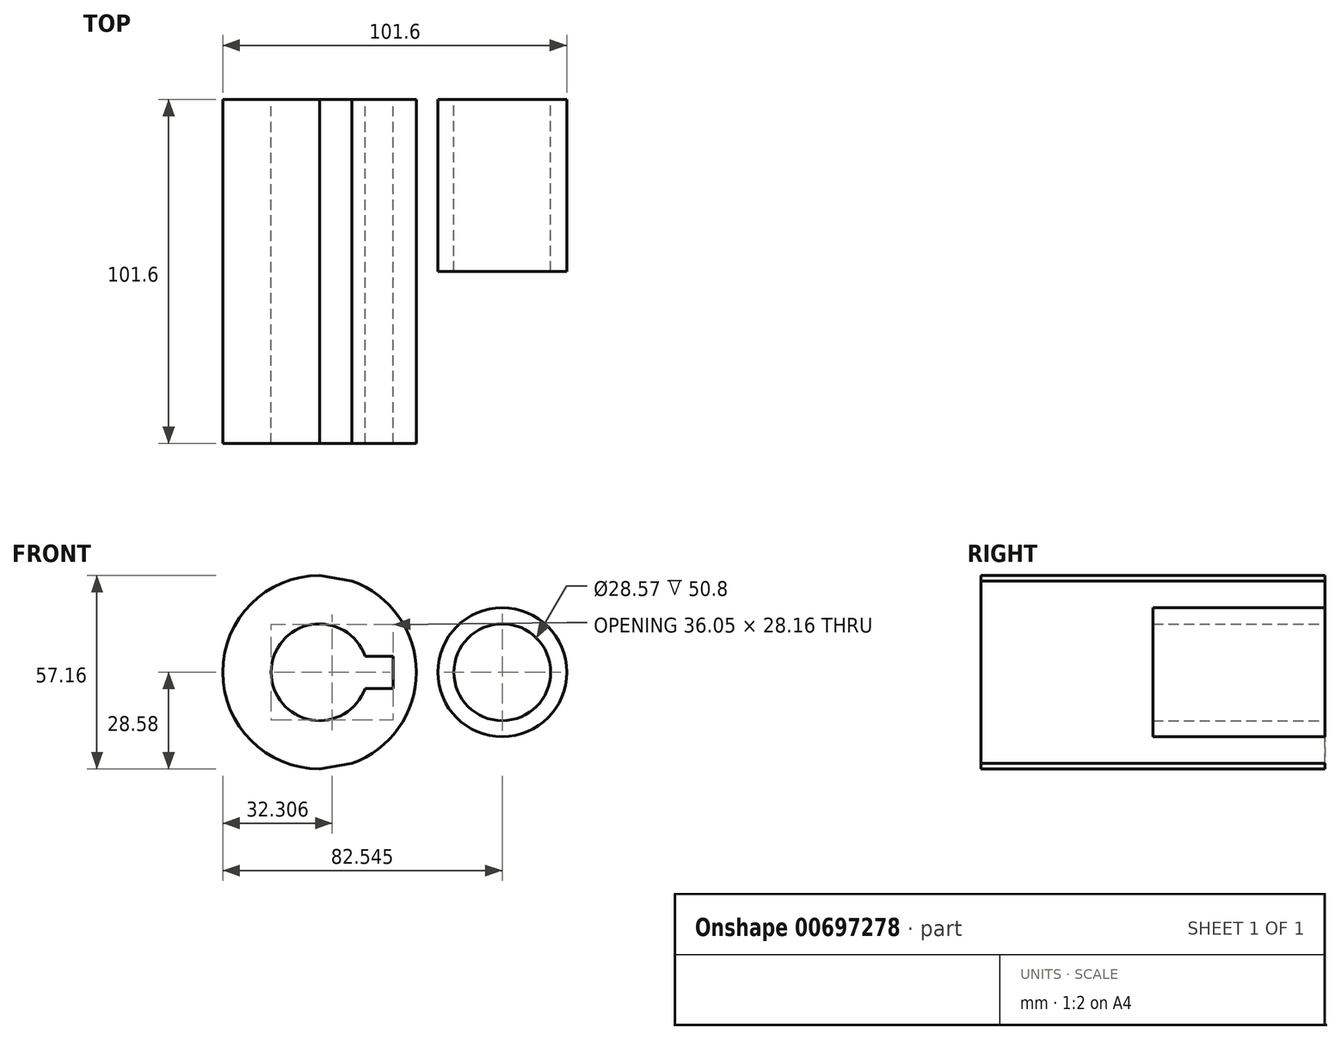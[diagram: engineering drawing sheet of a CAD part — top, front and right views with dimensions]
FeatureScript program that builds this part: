
annotation { "Feature Type Name" : "Feature", "Feature Type Description" : "" }
export const myFeature = defineFeature(function(context is Context, id is Id, definition is map)
    precondition{}
    {
        {
            var Q0;
            Q0=qCreatedBy(makeId("Front.planeOp"),FACE);
            var sketch = newSketch(context, id + "F0", { "sketchPlane" : qUnion([Q0])});
            skCircle(sketch, "E0", {"center": v(0, 0) * mm, "radius": 28.58 * mm});
            skCircle(sketch, "E1", {"center": v(53.98, 0) * mm, "radius": 19.05 * mm});
            skLineSegment(sketch, "E2", {"start": v(0, 28.57) * mm, "end": v(57.2, 18.78) * mm});
            skLineSegment(sketch, "E3", {"start": v(0, -28.58) * mm, "end": v(57.2, -18.78) * mm});
            skCircle(sketch, "E4", {"center": v(0, 0) * mm, "radius": 14.29 * mm});
            skCircle(sketch, "E5", {"center": v(53.98, 0) * mm, "radius": 14.29 * mm});
            skLineSegment(sketch, "E6.bottom", {"start": v(21.76, -4.76) * mm, "end": v(-21.76, -4.76) * mm});
            skLineSegment(sketch, "E6.top", {"start": v(21.76, 4.76) * mm, "end": v(-21.76, 4.76) * mm});
            skLineSegment(sketch, "E6.left", {"start": v(21.76, -4.76) * mm, "end": v(21.76, 4.76) * mm});
            skLineSegment(sketch, "E6.right", {"start": v(-21.76, -4.76) * mm, "end": v(-21.76, 4.76) * mm});
            skSolve(sketch);
        }
        {
            var Q0;
            {var subQ5=sQuery(id+"F0.wireOp",EDGE,"E6.right");Q0=makeQuery(id+"F0.imprint","IMPRINT",FACE,{"disambiguationData":[TD([[makeQuery(id+"F0.imprint","IMPRINT",EDGE,{"derivedFrom":subQ5}),-1.0]])]});}
            var Q1;
            Q1=makeQuery(id+"F0.imprint","IMPRINT",FACE,{"disambiguationData":[TD([[makeQuery(id+"F0.imprint","IMPRINT",EDGE,{"derivedFrom":sQuery(id+"F0.wireOp",EDGE,"E5")}),-1.0]])]});
            var Q2;
            {var subQ0=sQuery(id+"F0.wireOp",EDGE,"E2");var subQ1=sQuery(id+"F0.wireOp",EDGE,"E0");var subQ2=makeQuery(id+"F0.imprint","INTERSECT",VERTEX,{"disambiguationData":[OD(1.0)],"derivedFrom":[subQ1,subQ0]});Q2=makeQuery(id+"F0.imprint","IMPRINT",FACE,{"disambiguationData":[TD([[makeQuery(id+"F0.imprint","IMPRINT",EDGE,{"disambiguationData":[TD([[subQ2,1.0]])],"derivedFrom":subQ1}),-1.0]])]});}
            var Q3;
            {var subQ4=sQuery(id+"F0.wireOp",EDGE,"E6.left");Q3=makeQuery(id+"F0.imprint","IMPRINT",FACE,{"disambiguationData":[TD([[makeQuery(id+"F0.imprint","IMPRINT",EDGE,{"derivedFrom":subQ4}),-1.0]])]});}
            extrude(context, id + "F1", {"entities" : qUnion([Q0, Q1, Q2, Q3]), "depth" : 50.8 * mm, "offsetDistance" : 25.4 * mm});
        }
        {
            var Q0;
            {var subQ4=sQuery(id+"F0.wireOp",EDGE,"E6.left");Q0=makeQuery(id+"F0.imprint","IMPRINT",FACE,{"disambiguationData":[TD([[makeQuery(id+"F0.imprint","IMPRINT",EDGE,{"derivedFrom":subQ4}),-1.0]])]});}
            var Q1;
            {var subQ5=sQuery(id+"F0.wireOp",EDGE,"E6.right");Q1=makeQuery(id+"F0.imprint","IMPRINT",FACE,{"disambiguationData":[TD([[makeQuery(id+"F0.imprint","IMPRINT",EDGE,{"derivedFrom":subQ5}),-1.0]])]});}
            extrude(context, id + "F2", {"entities" : qUnion([Q0, Q1]), "operationType" : NewBodyOperationType.ADD, "depth" : 101.6 * mm, "offsetDistance" : 25.4 * mm});
        }
    });
